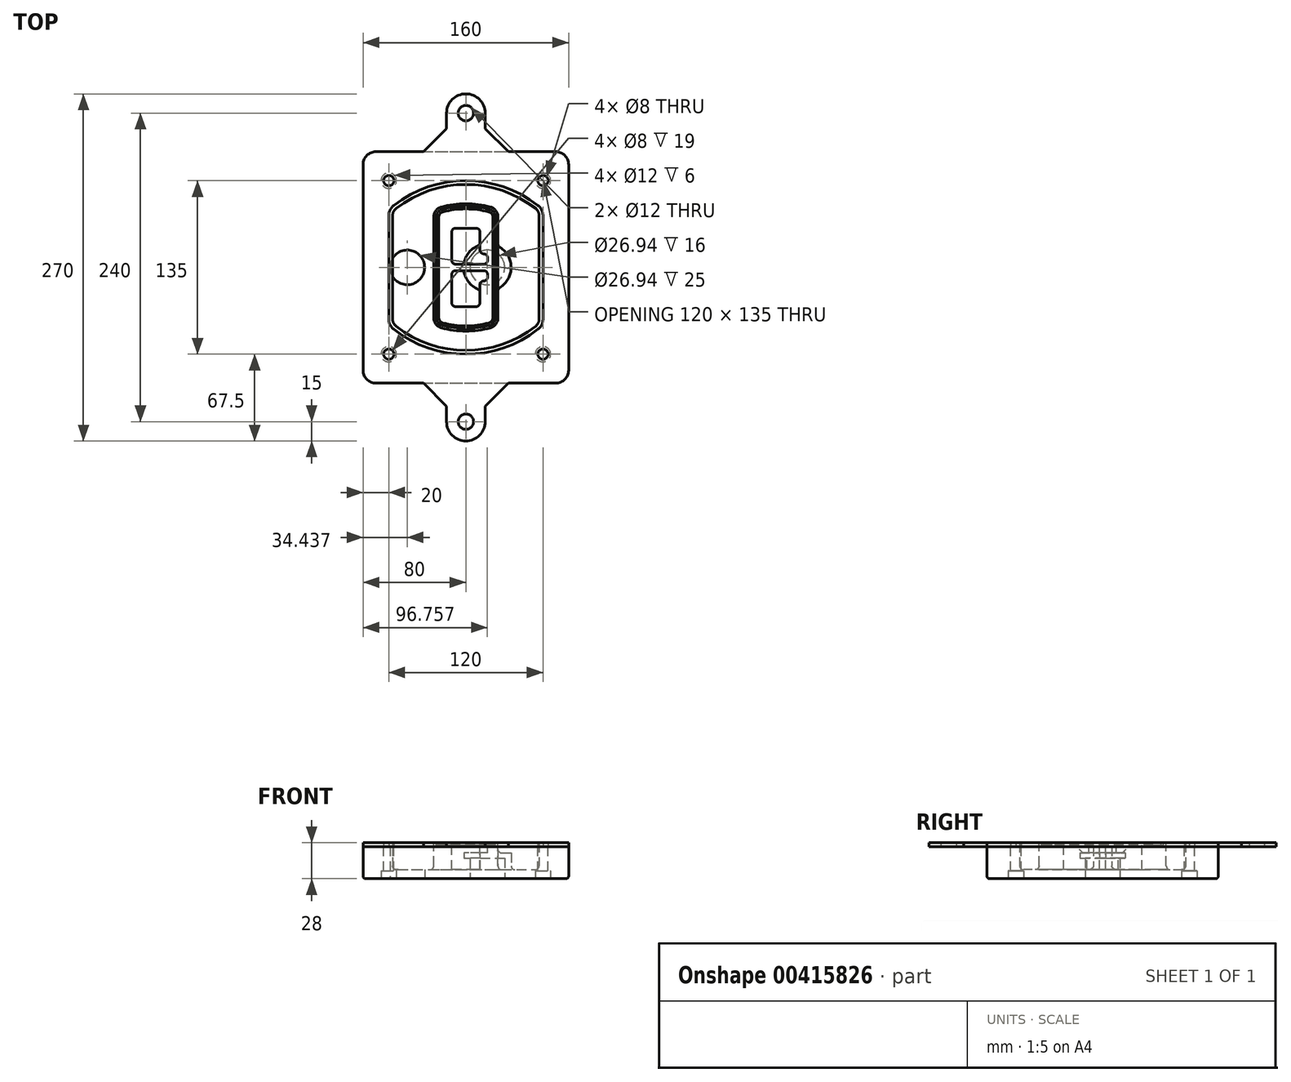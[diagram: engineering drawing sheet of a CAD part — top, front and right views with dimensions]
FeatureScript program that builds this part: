
annotation { "Feature Type Name" : "Feature", "Feature Type Description" : "" }
export const myFeature = defineFeature(function(context is Context, id is Id, definition is map)
    precondition{}
    {
        {
            var Q0;
            Q0=qCreatedBy(makeId("Top.planeOp"),FACE);
            var sketch = newSketch(context, id + "F0", { "sketchPlane" : qUnion([Q0])});
            skPoint(sketch, "E0.rect.middle", {"position": v(0, 0) * mm});
            skLineSegment(sketch, "E1.bottom", {"start": v(-70, -90) * mm, "end": v(70, -90) * mm});
            skLineSegment(sketch, "E1.top", {"start": v(-70, 90) * mm, "end": v(70, 90) * mm});
            skLineSegment(sketch, "E1.left", {"start": v(-80, -80) * mm, "end": v(-80, 80) * mm});
            skLineSegment(sketch, "E1.right", {"start": v(80, -80) * mm, "end": v(80, 80) * mm});
            skLineSegment(sketch, "E2", {"start": v(-80, 90) * mm, "end": v(80, -90) * mm, "construction": true});
            skLineSegment(sketch, "E3", {"start": v(80, 90) * mm, "end": v(-80, -90) * mm, "construction": true});
            skCircle(sketch, "E4", {"center": v(-60, 67.5) * mm, "radius": 4 * mm});
            skCircle(sketch, "E5", {"center": v(60, 67.5) * mm, "radius": 4 * mm});
            skCircle(sketch, "E6", {"center": v(60, -67.5) * mm, "radius": 4 * mm});
            skCircle(sketch, "E7", {"center": v(-60, -67.5) * mm, "radius": 4 * mm});
            skLineSegment(sketch, "E8", {"start": v(-60, 67.5) * mm, "end": v(60, 67.5) * mm, "construction": true});
            skLineSegment(sketch, "E9", {"start": v(60, 67.5) * mm, "end": v(60, -67.5) * mm, "construction": true});
            skLineSegment(sketch, "E10", {"start": v(60, -67.5) * mm, "end": v(-60, -67.5) * mm, "construction": true});
            skLineSegment(sketch, "E11", {"start": v(-60, -67.5) * mm, "end": v(-60, 67.5) * mm, "construction": true});
            skLineSegment(sketch, "E12", {"start": v(-60, 40.3) * mm, "end": v(-60, -40.3) * mm});
            skLineSegment(sketch, "E13", {"start": v(60, 40.3) * mm, "end": v(60, -40.3) * mm});
            skArc(sketch, "E14", {"start": v(56.15, 48.18) * mm, "mid": v(0, 67.5) * mm, "end": v(-56.15, 48.18) * mm});
            skArc(sketch, "E15", {"start": v(-56.15, -48.18) * mm, "mid": v(0, -67.5) * mm, "end": v(56.15, -48.18) * mm});
            skLineSegment(sketch, "E16", {"start": v(-60, 0) * mm, "end": v(60, 0) * mm, "construction": true});
            skPoint(sketch, "E17.visualSharp", {"position": v(-60, -45) * mm});
            skArc(sketch, "E17.filletArc", {"start": v(-60, -40.3) * mm, "mid": v(-58.99, -44.68) * mm, "end": v(-56.15, -48.18) * mm});
            skPoint(sketch, "E18.visualSharp", {"position": v(-60, 45) * mm});
            skArc(sketch, "E18.filletArc", {"start": v(-56.15, 48.18) * mm, "mid": v(-58.99, 44.68) * mm, "end": v(-60, 40.3) * mm});
            skPoint(sketch, "E19.visualSharp", {"position": v(60, 45) * mm});
            skArc(sketch, "E19.filletArc", {"start": v(60, 40.3) * mm, "mid": v(58.99, 44.68) * mm, "end": v(56.15, 48.18) * mm});
            skPoint(sketch, "E20.visualSharp", {"position": v(60, -45) * mm});
            skArc(sketch, "E20.filletArc", {"start": v(56.15, -48.18) * mm, "mid": v(58.99, -44.68) * mm, "end": v(60, -40.3) * mm});
            skPoint(sketch, "E21.visualSharp", {"position": v(-80, 90) * mm});
            skArc(sketch, "E21.filletArc", {"start": v(-70, 90) * mm, "mid": v(-77.07, 87.07) * mm, "end": v(-80, 80) * mm});
            skPoint(sketch, "E22.visualSharp", {"position": v(80, 90) * mm});
            skArc(sketch, "E22.filletArc", {"start": v(80, 80) * mm, "mid": v(77.07, 87.07) * mm, "end": v(70, 90) * mm});
            skPoint(sketch, "E23.visualSharp", {"position": v(80, -90) * mm});
            skArc(sketch, "E23.filletArc", {"start": v(70, -90) * mm, "mid": v(77.07, -87.07) * mm, "end": v(80, -80) * mm});
            skPoint(sketch, "E24.visualSharp", {"position": v(-80, -90) * mm});
            skArc(sketch, "E24.filletArc", {"start": v(-80, -80) * mm, "mid": v(-77.07, -87.07) * mm, "end": v(-70, -90) * mm});
            skArc(sketch, "E25.0", {"start": v(57, 40.3) * mm, "mid": v(56.3, 43.36) * mm, "end": v(54.3, 45.81) * mm});
            skLineSegment(sketch, "E25.1", {"start": v(57, 40.3) * mm, "end": v(57, -40.3) * mm});
            skArc(sketch, "E25.2", {"start": v(54.3, -45.81) * mm, "mid": v(56.3, -43.36) * mm, "end": v(57, -40.3) * mm});
            skArc(sketch, "E25.3", {"start": v(-54.3, -45.81) * mm, "mid": v(0, -64.5) * mm, "end": v(54.3, -45.81) * mm});
            skArc(sketch, "E25.4", {"start": v(-57, -40.3) * mm, "mid": v(-56.3, -43.36) * mm, "end": v(-54.3, -45.81) * mm});
            skArc(sketch, "E25.5", {"start": v(54.3, 45.81) * mm, "mid": v(0, 64.5) * mm, "end": v(-54.3, 45.81) * mm});
            skLineSegment(sketch, "E25.6", {"start": v(-57, 40.3) * mm, "end": v(-57, -40.3) * mm});
            skArc(sketch, "E25.7", {"start": v(-54.3, 45.81) * mm, "mid": v(-56.3, 43.36) * mm, "end": v(-57, 40.3) * mm});
            skArc(sketch, "E26.0", {"start": v(-58.62, 51.33) * mm, "mid": v(-62.58, 46.43) * mm, "end": v(-64, 40.3) * mm});
            skArc(sketch, "E26.1", {"start": v(58.62, 51.33) * mm, "mid": v(0, 71.5) * mm, "end": v(-58.62, 51.33) * mm});
            skArc(sketch, "E26.2", {"start": v(64, 40.3) * mm, "mid": v(62.58, 46.43) * mm, "end": v(58.62, 51.33) * mm});
            skLineSegment(sketch, "E26.3", {"start": v(64, 40.3) * mm, "end": v(64, -40.3) * mm});
            skArc(sketch, "E26.4", {"start": v(58.62, -51.33) * mm, "mid": v(62.58, -46.43) * mm, "end": v(64, -40.3) * mm});
            skLineSegment(sketch, "E26.5", {"start": v(-64, 40.3) * mm, "end": v(-64, -40.3) * mm});
            skArc(sketch, "E26.6", {"start": v(-58.62, -51.33) * mm, "mid": v(0, -71.5) * mm, "end": v(58.62, -51.33) * mm});
            skArc(sketch, "E26.7", {"start": v(-64, -40.3) * mm, "mid": v(-62.58, -46.43) * mm, "end": v(-58.62, -51.33) * mm});
            skSolve(sketch);
        }
        {
            var Q0;
            Q0=makeQuery(id+"F0.imprint","IMPRINT",FACE,{"disambiguationData":[TD([[makeQuery(id+"F0.imprint","IMPRINT",EDGE,{"derivedFrom":sQuery(id+"F0.wireOp",EDGE,"E1.bottom")}),1.0]])]});
            var Q1;
            Q1=makeQuery(id+"F0.imprint","IMPRINT",FACE,{"disambiguationData":[TD([[makeQuery(id+"F0.imprint","IMPRINT",EDGE,{"derivedFrom":sQuery(id+"F0.wireOp",EDGE,"E12")}),1.0]])]});
            var Q2;
            Q2=makeQuery(id+"F0.imprint","IMPRINT",FACE,{"disambiguationData":[TD([[makeQuery(id+"F0.imprint","IMPRINT",EDGE,{"derivedFrom":sQuery(id+"F0.wireOp",EDGE,"E25.0")}),1.0]])]});
            var Q3;
            Q3=makeQuery(id+"F0.imprint","IMPRINT",FACE,{"disambiguationData":[TD([[makeQuery(id+"F0.imprint","IMPRINT",EDGE,{"derivedFrom":sQuery(id+"F0.wireOp",EDGE,"E12")}),-1.0]])]});
            extrude(context, id + "F1", {"entities" : qUnion([Q0, Q1, Q2, Q3]), "oppositeDirection" : true, "depth" : 25 * mm});
        }
        {
            var Q0;
            Q0=makeQuery(id+"F0.imprint","IMPRINT",FACE,{"disambiguationData":[TD([[makeQuery(id+"F0.imprint","IMPRINT",EDGE,{"derivedFrom":sQuery(id+"F0.wireOp",EDGE,"E12")}),1.0]])]});
            extrude(context, id + "F2", {"entities" : qUnion([Q0]), "operationType" : NewBodyOperationType.ADD, "depth" : 3 * mm});
        }
        {
            var Q0;
            Q0=makeQuery(id+"F0.imprint","IMPRINT",FACE,{"disambiguationData":[TD([[makeQuery(id+"F0.imprint","IMPRINT",EDGE,{"derivedFrom":sQuery(id+"F0.wireOp",EDGE,"E25.0")}),1.0]])]});
            extrude(context, id + "F3", {"entities" : qUnion([Q0]), "operationType" : NewBodyOperationType.REMOVE, "oppositeDirection" : true, "depth" : 18 * mm});
        }
        {
            var Q0;
            Q0=makeQuery(id+"F2.opExtrude","CAP_FACE",FACE,{"disambiguationData":[OSD([sQuery(id+"F0.wireOp",EDGE,"E12"),sQuery(id+"F0.wireOp",EDGE,"E13"),sQuery(id+"F0.wireOp",EDGE,"E14"),sQuery(id+"F0.wireOp",EDGE,"E15"),sQuery(id+"F0.wireOp",EDGE,"E17.filletArc"),sQuery(id+"F0.wireOp",EDGE,"E18.filletArc"),sQuery(id+"F0.wireOp",EDGE,"E19.filletArc"),sQuery(id+"F0.wireOp",EDGE,"E20.filletArc"),sQuery(id+"F0.wireOp",EDGE,"E25.0"),sQuery(id+"F0.wireOp",EDGE,"E25.1"),sQuery(id+"F0.wireOp",EDGE,"E25.2"),sQuery(id+"F0.wireOp",EDGE,"E25.3"),sQuery(id+"F0.wireOp",EDGE,"E25.4"),sQuery(id+"F0.wireOp",EDGE,"E25.5"),sQuery(id+"F0.wireOp",EDGE,"E25.6"),sQuery(id+"F0.wireOp",EDGE,"E25.7")])],"isStart":false});
            var sketch = newSketch(context, id + "F4", { "sketchPlane" : qUnion([Q0])});
            skArc(sketch, "E27.0", {"start": v(-19.08, -46.97) * mm, "mid": v(0, -49.5) * mm, "end": v(19.08, -46.97) * mm});
            skArc(sketch, "E28.0", {"start": v(19.08, 46.97) * mm, "mid": v(0, 49.5) * mm, "end": v(-19.08, 46.97) * mm});
            skLineSegment(sketch, "E29", {"start": v(-25, 39.25) * mm, "end": v(-25, -39.25) * mm});
            skLineSegment(sketch, "E30", {"start": v(25, 39.25) * mm, "end": v(25, -39.25) * mm});
            skLineSegment(sketch, "E31", {"start": v(-25, 45.1) * mm, "end": v(25, 45.1) * mm, "construction": true});
            skLineSegment(sketch, "E32", {"start": v(-25, -45.1) * mm, "end": v(25, -45.1) * mm, "construction": true});
            skPoint(sketch, "E33.visualSharp", {"position": v(-25, 45.1) * mm});
            skArc(sketch, "E33.filletArc", {"start": v(-19.08, 46.97) * mm, "mid": v(-23.35, 44.11) * mm, "end": v(-25, 39.25) * mm});
            skPoint(sketch, "E34.visualSharp", {"position": v(25, 45.1) * mm});
            skArc(sketch, "E34.filletArc", {"start": v(25, 39.25) * mm, "mid": v(23.35, 44.11) * mm, "end": v(19.08, 46.97) * mm});
            skPoint(sketch, "E35.visualSharp", {"position": v(25, -45.1) * mm});
            skArc(sketch, "E35.filletArc", {"start": v(19.08, -46.97) * mm, "mid": v(23.35, -44.11) * mm, "end": v(25, -39.25) * mm});
            skPoint(sketch, "E36.visualSharp", {"position": v(-25, -45.1) * mm});
            skArc(sketch, "E36.filletArc", {"start": v(-25, -39.25) * mm, "mid": v(-23.35, -44.11) * mm, "end": v(-19.08, -46.97) * mm});
            skArc(sketch, "E37.0", {"start": v(54.3, 45.81) * mm, "mid": v(0, 64.5) * mm, "end": v(-54.3, 45.81) * mm});
            skArc(sketch, "E37.1", {"start": v(-54.3, 45.81) * mm, "mid": v(-56.3, 43.36) * mm, "end": v(-57, 40.3) * mm});
            skLineSegment(sketch, "E37.2", {"start": v(-57, 40.3) * mm, "end": v(-57, -40.3) * mm});
            skArc(sketch, "E37.3", {"start": v(-57, -40.3) * mm, "mid": v(-56.3, -43.36) * mm, "end": v(-54.3, -45.81) * mm});
            skArc(sketch, "E37.4", {"start": v(-54.3, -45.81) * mm, "mid": v(0, -64.5) * mm, "end": v(54.3, -45.81) * mm});
            skArc(sketch, "E37.5", {"start": v(54.3, -45.81) * mm, "mid": v(56.3, -43.36) * mm, "end": v(57, -40.3) * mm});
            skLineSegment(sketch, "E37.6", {"start": v(57, 40.3) * mm, "end": v(57, -40.3) * mm});
            skArc(sketch, "E37.7", {"start": v(57, 40.3) * mm, "mid": v(56.3, 43.36) * mm, "end": v(54.3, 45.81) * mm});
            skLineSegment(sketch, "E38.0", {"start": v(23, 39.25) * mm, "end": v(23, -39.25) * mm});
            skArc(sketch, "E38.1", {"start": v(18.56, -45.04) * mm, "mid": v(21.76, -42.9) * mm, "end": v(23, -39.25) * mm});
            skArc(sketch, "E38.2", {"start": v(-18.56, -45.04) * mm, "mid": v(0, -47.5) * mm, "end": v(18.56, -45.04) * mm});
            skArc(sketch, "E38.3", {"start": v(-23, -39.25) * mm, "mid": v(-21.76, -42.9) * mm, "end": v(-18.56, -45.04) * mm});
            skLineSegment(sketch, "E38.4", {"start": v(-23, 39.25) * mm, "end": v(-23, -39.25) * mm});
            skArc(sketch, "E38.5", {"start": v(23, 39.25) * mm, "mid": v(21.76, 42.9) * mm, "end": v(18.56, 45.04) * mm});
            skArc(sketch, "E38.6", {"start": v(-18.56, 45.04) * mm, "mid": v(-21.76, 42.9) * mm, "end": v(-23, 39.25) * mm});
            skArc(sketch, "E38.7", {"start": v(18.56, 45.04) * mm, "mid": v(0, 47.5) * mm, "end": v(-18.56, 45.04) * mm});
            skArc(sketch, "E39.0", {"start": v(21, 39.25) * mm, "mid": v(20.18, 41.68) * mm, "end": v(18.04, 43.1) * mm});
            skLineSegment(sketch, "E39.1", {"start": v(21, 39.25) * mm, "end": v(21, -39.25) * mm});
            skArc(sketch, "E39.2", {"start": v(18.04, -43.1) * mm, "mid": v(20.18, -41.68) * mm, "end": v(21, -39.25) * mm});
            skArc(sketch, "E39.3", {"start": v(-18.04, -43.1) * mm, "mid": v(0, -45.5) * mm, "end": v(18.04, -43.1) * mm});
            skArc(sketch, "E39.4", {"start": v(-21, -39.25) * mm, "mid": v(-20.18, -41.68) * mm, "end": v(-18.04, -43.1) * mm});
            skArc(sketch, "E39.5", {"start": v(18.04, 43.1) * mm, "mid": v(0, 45.5) * mm, "end": v(-18.04, 43.1) * mm});
            skLineSegment(sketch, "E39.6", {"start": v(-21, 39.25) * mm, "end": v(-21, -39.25) * mm});
            skArc(sketch, "E39.7", {"start": v(-18.04, 43.1) * mm, "mid": v(-20.18, 41.68) * mm, "end": v(-21, 39.25) * mm});
            skLineSegment(sketch, "E40", {"start": v(-25, 0) * mm, "end": v(25, 0) * mm, "construction": true});
            skLineSegment(sketch, "E41", {"start": v(-11, 5.5) * mm, "end": v(-11, 27.5) * mm});
            skLineSegment(sketch, "E42", {"start": v(-8, 30.5) * mm, "end": v(8, 30.5) * mm});
            skLineSegment(sketch, "E43", {"start": v(11, 27.5) * mm, "end": v(11, 13.5) * mm});
            skLineSegment(sketch, "E44", {"start": v(14, 10.5) * mm, "end": v(14, 10.5) * mm});
            skLineSegment(sketch, "E45", {"start": v(17, 7.5) * mm, "end": v(17, 5.5) * mm});
            skLineSegment(sketch, "E46", {"start": v(14, 2.5) * mm, "end": v(-8, 2.5) * mm});
            skPoint(sketch, "E47.visualSharp", {"position": v(-11, 30.5) * mm});
            skArc(sketch, "E47.filletArc", {"start": v(-8, 30.5) * mm, "mid": v(-10.12, 29.62) * mm, "end": v(-11, 27.5) * mm});
            skPoint(sketch, "E48.visualSharp", {"position": v(11, 30.5) * mm});
            skArc(sketch, "E48.filletArc", {"start": v(11, 27.5) * mm, "mid": v(10.12, 29.62) * mm, "end": v(8, 30.5) * mm});
            skPoint(sketch, "E49.visualSharp", {"position": v(11, 10.5) * mm});
            skArc(sketch, "E49.filletArc", {"start": v(11, 13.5) * mm, "mid": v(11.88, 11.38) * mm, "end": v(14, 10.5) * mm});
            skPoint(sketch, "E50.visualSharp", {"position": v(17, 10.5) * mm});
            skArc(sketch, "E50.filletArc", {"start": v(17, 7.5) * mm, "mid": v(16.12, 9.62) * mm, "end": v(14, 10.5) * mm});
            skPoint(sketch, "E51.visualSharp", {"position": v(17, 2.5) * mm});
            skArc(sketch, "E51.filletArc", {"start": v(14, 2.5) * mm, "mid": v(16.12, 3.38) * mm, "end": v(17, 5.5) * mm});
            skPoint(sketch, "E52.visualSharp", {"position": v(-11, 2.5) * mm});
            skArc(sketch, "E52.filletArc", {"start": v(-11, 5.5) * mm, "mid": v(-10.12, 3.38) * mm, "end": v(-8, 2.5) * mm});
            skLineSegment(sketch, "E53.0.MirrorCS", {"start": v(14, -2.5) * mm, "end": v(-8, -2.5) * mm});
            skArc(sketch, "E54.0.MirrorCS", {"start": v(-11, -5.5) * mm, "mid": v(-10.12, -3.38) * mm, "end": v(-8, -2.5) * mm});
            skLineSegment(sketch, "E55.0.MirrorCS", {"start": v(-11, -5.5) * mm, "end": v(-11, -27.5) * mm});
            skArc(sketch, "E56.0.MirrorCS", {"start": v(-8, -30.5) * mm, "mid": v(-10.12, -29.62) * mm, "end": v(-11, -27.5) * mm});
            skLineSegment(sketch, "E57.0.MirrorCS", {"start": v(-8, -30.5) * mm, "end": v(8, -30.5) * mm});
            skArc(sketch, "E58.0.MirrorCS", {"start": v(11, -27.5) * mm, "mid": v(10.12, -29.62) * mm, "end": v(8, -30.5) * mm});
            skLineSegment(sketch, "E59.0.MirrorCS", {"start": v(11, -27.5) * mm, "end": v(11, -13.5) * mm});
            skArc(sketch, "E60.0.MirrorCS", {"start": v(11, -13.5) * mm, "mid": v(11.88, -11.38) * mm, "end": v(14, -10.5) * mm});
            skArc(sketch, "E61.0.MirrorCS", {"start": v(17, -7.5) * mm, "mid": v(16.12, -9.62) * mm, "end": v(14, -10.5) * mm});
            skLineSegment(sketch, "E62.0.MirrorCS", {"start": v(17, -7.5) * mm, "end": v(17, -5.5) * mm});
            skArc(sketch, "E63.0.MirrorCS", {"start": v(14, -2.5) * mm, "mid": v(16.12, -3.38) * mm, "end": v(17, -5.5) * mm});
            skSolve(sketch);
        }
        {
            var Q0;
            Q0=makeQuery(id+"F4.imprint","IMPRINT",FACE,{"disambiguationData":[TD([[makeQuery(id+"F4.imprint","IMPRINT",EDGE,{"derivedFrom":sQuery(id+"F4.wireOp",EDGE,"E27.0")}),1.0]])]});
            var Q1;
            Q1=makeQuery(id+"F4.imprint","IMPRINT",FACE,{"disambiguationData":[TD([[makeQuery(id+"F4.imprint","IMPRINT",EDGE,{"derivedFrom":sQuery(id+"F4.wireOp",EDGE,"E38.0")}),-1.0]])]});
            var Q2;
            Q2=makeQuery(id+"F4.imprint","IMPRINT",FACE,{"disambiguationData":[TD([[makeQuery(id+"F4.imprint","IMPRINT",EDGE,{"derivedFrom":sQuery(id+"F4.wireOp",EDGE,"E39.0")}),1.0]])]});
            extrude(context, id + "F5", {"entities" : qUnion([Q0, Q1, Q2]), "operationType" : NewBodyOperationType.ADD, "endBound" : BoundingType.UP_TO_NEXT, "oppositeDirection" : true, "depth" : 25 * mm});
        }
        {
            var Q0;
            Q0=makeQuery(id+"F4.imprint","IMPRINT",FACE,{"disambiguationData":[TD([[makeQuery(id+"F4.imprint","IMPRINT",EDGE,{"derivedFrom":sQuery(id+"F4.wireOp",EDGE,"E38.0")}),-1.0]])]});
            extrude(context, id + "F6", {"entities" : qUnion([Q0]), "operationType" : NewBodyOperationType.REMOVE, "oppositeDirection" : true, "depth" : 2 * mm});
        }
        {
            var Q0;
            Q0=makeQuery(id+"F1.opExtrude","CAP_FACE",FACE,{"disambiguationData":[OSD([sQuery(id+"F0.wireOp",EDGE,"E1.bottom"),sQuery(id+"F0.wireOp",EDGE,"E1.top"),sQuery(id+"F0.wireOp",EDGE,"E1.left"),sQuery(id+"F0.wireOp",EDGE,"E1.right"),sQuery(id+"F0.wireOp",EDGE,"E4"),sQuery(id+"F0.wireOp",EDGE,"E5"),sQuery(id+"F0.wireOp",EDGE,"E6"),sQuery(id+"F0.wireOp",EDGE,"E7"),sQuery(id+"F0.wireOp",EDGE,"E21.filletArc"),sQuery(id+"F0.wireOp",EDGE,"E22.filletArc"),sQuery(id+"F0.wireOp",EDGE,"E23.filletArc"),sQuery(id+"F0.wireOp",EDGE,"E24.filletArc")])],"isStart":false});
            var sketch = newSketch(context, id + "F7", { "sketchPlane" : qUnion([Q0])});
            skCircle(sketch, "E64", {"center": v(16.76, 0) * mm, "radius": 13.47 * mm});
            skCircle(sketch, "E65", {"center": v(-45.56, 0) * mm, "radius": 13.47 * mm});
            skLineSegment(sketch, "E66", {"start": v(80, 0) * mm, "end": v(-80, 0) * mm});
            skCircle(sketch, "E67", {"center": v(16.76, 0) * mm, "radius": 18.47 * mm});
            skCircle(sketch, "E68", {"center": v(60, -67.5) * mm, "radius": 6 * mm});
            skCircle(sketch, "E69", {"center": v(-60, -67.5) * mm, "radius": 6 * mm});
            skCircle(sketch, "E70", {"center": v(-60, 67.5) * mm, "radius": 6 * mm});
            skCircle(sketch, "E71", {"center": v(60, 67.5) * mm, "radius": 6 * mm});
            skSolve(sketch);
        }
        {
            var Q0;
            {var subQ1=sQuery(id+"F7.wireOp",EDGE,"E66");var subQ4=sQuery(id+"F7.wireOp",EDGE,"E64");var subQ6=makeQuery(id+"F7.imprint","INTERSECT",VERTEX,{"disambiguationData":[OD(0.0)],"derivedFrom":[subQ4,subQ1]});Q0=makeQuery(id+"F7.imprint","IMPRINT",FACE,{"disambiguationData":[TD([[makeQuery(id+"F7.imprint","IMPRINT",EDGE,{"disambiguationData":[TD([[subQ6,-1.0]])],"derivedFrom":subQ4}),-1.0]])]});}
            var Q1;
            {var subQ0=sQuery(id+"F7.wireOp",EDGE,"E66");var subQ1=sQuery(id+"F7.wireOp",EDGE,"E64");var subQ3=makeQuery(id+"F7.imprint","INTERSECT",VERTEX,{"disambiguationData":[OD(0.0)],"derivedFrom":[subQ1,subQ0]});Q1=makeQuery(id+"F7.imprint","IMPRINT",FACE,{"disambiguationData":[TD([[makeQuery(id+"F7.imprint","IMPRINT",EDGE,{"disambiguationData":[TD([[subQ3,-1.0]])],"derivedFrom":subQ1}),1.0]])]});}
            var Q2;
            {var subQ0=sQuery(id+"F7.wireOp",EDGE,"E66");var subQ1=sQuery(id+"F7.wireOp",EDGE,"E64");var subQ3=makeQuery(id+"F7.imprint","INTERSECT",VERTEX,{"disambiguationData":[OD(0.0)],"derivedFrom":[subQ1,subQ0]});Q2=makeQuery(id+"F7.imprint","IMPRINT",FACE,{"disambiguationData":[TD([[makeQuery(id+"F7.imprint","IMPRINT",EDGE,{"disambiguationData":[TD([[subQ3,1.0]])],"derivedFrom":subQ1}),1.0]])]});}
            var Q3;
            {var subQ1=sQuery(id+"F7.wireOp",EDGE,"E66");var subQ4=sQuery(id+"F7.wireOp",EDGE,"E64");var subQ6=makeQuery(id+"F7.imprint","INTERSECT",VERTEX,{"disambiguationData":[OD(0.0)],"derivedFrom":[subQ4,subQ1]});Q3=makeQuery(id+"F7.imprint","IMPRINT",FACE,{"disambiguationData":[TD([[makeQuery(id+"F7.imprint","IMPRINT",EDGE,{"disambiguationData":[TD([[subQ6,1.0]])],"derivedFrom":subQ4}),-1.0]])]});}
            extrude(context, id + "F8", {"entities" : qUnion([Q0, Q1, Q2, Q3]), "operationType" : NewBodyOperationType.ADD, "oppositeDirection" : true, "depth" : 20 * mm});
        }
        {
            var Q0;
            {var subQ0=sQuery(id+"F7.wireOp",EDGE,"E66");var subQ1=sQuery(id+"F7.wireOp",EDGE,"E64");var subQ3=makeQuery(id+"F7.imprint","INTERSECT",VERTEX,{"disambiguationData":[OD(0.0)],"derivedFrom":[subQ1,subQ0]});Q0=makeQuery(id+"F7.imprint","IMPRINT",FACE,{"disambiguationData":[TD([[makeQuery(id+"F7.imprint","IMPRINT",EDGE,{"disambiguationData":[TD([[subQ3,-1.0]])],"derivedFrom":subQ1}),1.0]])]});}
            var Q1;
            {var subQ0=sQuery(id+"F7.wireOp",EDGE,"E66");var subQ1=sQuery(id+"F7.wireOp",EDGE,"E64");var subQ3=makeQuery(id+"F7.imprint","INTERSECT",VERTEX,{"disambiguationData":[OD(0.0)],"derivedFrom":[subQ1,subQ0]});Q1=makeQuery(id+"F7.imprint","IMPRINT",FACE,{"disambiguationData":[TD([[makeQuery(id+"F7.imprint","IMPRINT",EDGE,{"disambiguationData":[TD([[subQ3,1.0]])],"derivedFrom":subQ1}),1.0]])]});}
            extrude(context, id + "F9", {"entities" : qUnion([Q0, Q1]), "operationType" : NewBodyOperationType.REMOVE, "oppositeDirection" : true, "depth" : 16 * mm});
        }
        {
            var Q0;
            {var subQ0=sQuery(id+"F7.wireOp",EDGE,"E66");var subQ1=sQuery(id+"F7.wireOp",EDGE,"E65");var subQ3=makeQuery(id+"F7.imprint","INTERSECT",VERTEX,{"disambiguationData":[OD(0.0)],"derivedFrom":[subQ1,subQ0]});Q0=makeQuery(id+"F7.imprint","IMPRINT",FACE,{"disambiguationData":[TD([[makeQuery(id+"F7.imprint","IMPRINT",EDGE,{"disambiguationData":[TD([[subQ3,-1.0]])],"derivedFrom":subQ1}),1.0]])]});}
            var Q1;
            {var subQ0=sQuery(id+"F7.wireOp",EDGE,"E66");var subQ1=sQuery(id+"F7.wireOp",EDGE,"E65");var subQ3=makeQuery(id+"F7.imprint","INTERSECT",VERTEX,{"disambiguationData":[OD(0.0)],"derivedFrom":[subQ1,subQ0]});Q1=makeQuery(id+"F7.imprint","IMPRINT",FACE,{"disambiguationData":[TD([[makeQuery(id+"F7.imprint","IMPRINT",EDGE,{"disambiguationData":[TD([[subQ3,1.0]])],"derivedFrom":subQ1}),1.0]])]});}
            extrude(context, id + "F10", {"entities" : qUnion([Q0, Q1]), "operationType" : NewBodyOperationType.REMOVE, "oppositeDirection" : true, "depth" : 25 * mm});
        }
        {
            var Q0;
            Q0=makeQuery(id+"F7.imprint","IMPRINT",FACE,{"disambiguationData":[TD([[makeQuery(id+"F7.imprint","IMPRINT",EDGE,{"derivedFrom":sQuery(id+"F7.wireOp",EDGE,"E68")}),1.0]])]});
            var Q1;
            Q1=makeQuery(id+"F7.imprint","IMPRINT",FACE,{"disambiguationData":[TD([[makeQuery(id+"F7.imprint","IMPRINT",EDGE,{"derivedFrom":makeQuery(id+"F1.opExtrude","CAP_EDGE",EDGE,{"disambiguationData":[OSD([sQuery(id+"F0.wireOp",EDGE,"E5")])],"isStart":false})}),-1.0]])]});
            var Q2;
            Q2=makeQuery(id+"F7.imprint","IMPRINT",FACE,{"disambiguationData":[TD([[makeQuery(id+"F7.imprint","IMPRINT",EDGE,{"derivedFrom":sQuery(id+"F7.wireOp",EDGE,"E69")}),1.0]])]});
            var Q3;
            Q3=makeQuery(id+"F7.imprint","IMPRINT",FACE,{"disambiguationData":[TD([[makeQuery(id+"F7.imprint","IMPRINT",EDGE,{"derivedFrom":makeQuery(id+"F1.opExtrude","CAP_EDGE",EDGE,{"disambiguationData":[OSD([sQuery(id+"F0.wireOp",EDGE,"E4")])],"isStart":false})}),-1.0]])]});
            var Q4;
            Q4=makeQuery(id+"F7.imprint","IMPRINT",FACE,{"disambiguationData":[TD([[makeQuery(id+"F7.imprint","IMPRINT",EDGE,{"derivedFrom":sQuery(id+"F7.wireOp",EDGE,"E70")}),1.0]])]});
            var Q5;
            Q5=makeQuery(id+"F7.imprint","IMPRINT",FACE,{"disambiguationData":[TD([[makeQuery(id+"F7.imprint","IMPRINT",EDGE,{"derivedFrom":makeQuery(id+"F1.opExtrude","CAP_EDGE",EDGE,{"disambiguationData":[OSD([sQuery(id+"F0.wireOp",EDGE,"E7")])],"isStart":false})}),-1.0]])]});
            var Q6;
            Q6=makeQuery(id+"F7.imprint","IMPRINT",FACE,{"disambiguationData":[TD([[makeQuery(id+"F7.imprint","IMPRINT",EDGE,{"derivedFrom":sQuery(id+"F7.wireOp",EDGE,"E71")}),1.0]])]});
            var Q7;
            Q7=makeQuery(id+"F7.imprint","IMPRINT",FACE,{"disambiguationData":[TD([[makeQuery(id+"F7.imprint","IMPRINT",EDGE,{"derivedFrom":makeQuery(id+"F1.opExtrude","CAP_EDGE",EDGE,{"disambiguationData":[OSD([sQuery(id+"F0.wireOp",EDGE,"E6")])],"isStart":false})}),-1.0]])]});
            extrude(context, id + "F11", {"entities" : qUnion([Q0, Q1, Q2, Q3, Q4, Q5, Q6, Q7]), "operationType" : NewBodyOperationType.REMOVE, "oppositeDirection" : true, "depth" : 6 * mm});
        }
        {
            var Q0;
            Q0=makeQuery(id+"F9.boolean.opBoolean","COPY",FACE,{"derivedFrom":makeQuery(id+"F9.opExtrude","CAP_FACE",FACE,{"disambiguationData":[OSD([sQuery(id+"F7.wireOp",EDGE,"E64")])],"isStart":false})});
            var sketch = newSketch(context, id + "F12", { "sketchPlane" : qUnion([Q0])});
            skArc(sketch, "E72.0", {"start": v(11, 17.55) * mm, "mid": v(2.57, 11.82) * mm, "end": v(-1.54, 2.5) * mm});
            skArc(sketch, "E72.1", {"start": v(-1.54, -2.5) * mm, "mid": v(2.57, -11.82) * mm, "end": v(11, -17.55) * mm});
            skLineSegment(sketch, "E73", {"start": v(-1.54, -2.5) * mm, "end": v(14, -2.5) * mm});
            skLineSegment(sketch, "E74.0", {"start": v(14, 2.5) * mm, "end": v(-1.54, 2.5) * mm});
            skArc(sketch, "E74.1", {"start": v(14, 2.5) * mm, "mid": v(16.12, 3.38) * mm, "end": v(17, 5.5) * mm});
            skLineSegment(sketch, "E74.2", {"start": v(17, 7.5) * mm, "end": v(17, 5.5) * mm});
            skArc(sketch, "E74.3", {"start": v(17, 7.5) * mm, "mid": v(16.12, 9.62) * mm, "end": v(14, 10.5) * mm});
            skArc(sketch, "E74.4", {"start": v(11, 13.5) * mm, "mid": v(11.88, 11.38) * mm, "end": v(14, 10.5) * mm});
            skLineSegment(sketch, "E74.5", {"start": v(11, 17.55) * mm, "end": v(11, 13.5) * mm});
            skLineSegment(sketch, "E74.7", {"start": v(14, -2.5) * mm, "end": v(-1.54, -2.5) * mm});
            skArc(sketch, "E74.8", {"start": v(14, -2.5) * mm, "mid": v(16.12, -3.38) * mm, "end": v(17, -5.5) * mm});
            skLineSegment(sketch, "E74.9", {"start": v(17, -7.5) * mm, "end": v(17, -5.5) * mm});
            skArc(sketch, "E74.10", {"start": v(17, -7.5) * mm, "mid": v(16.12, -9.62) * mm, "end": v(14, -10.5) * mm});
            skArc(sketch, "E74.11", {"start": v(11, -13.5) * mm, "mid": v(11.88, -11.38) * mm, "end": v(14, -10.5) * mm});
            skLineSegment(sketch, "E74.12", {"start": v(11, -17.55) * mm, "end": v(11, -13.5) * mm});
            skPoint(sketch, "E75.orphan", {"position": v(11, -27.5) * mm});
            skPoint(sketch, "E76.orphan", {"position": v(-8, -2.5) * mm});
            skPoint(sketch, "E77.orphan", {"position": v(-8, 2.5) * mm});
            skPoint(sketch, "E78.orphan", {"position": v(11, 27.5) * mm});
            skSolve(sketch);
        }
        {
            var Q0;
            {var subQ7=sQuery(id+"F12.wireOp",EDGE,"E72.0");var subQ14=sQuery(id+"F12.wireOp",EDGE,"E72.1");var subQ16=sQuery(id+"F12.wireOp",EDGE,"E74.1");var subQ18=sQuery(id+"F12.wireOp",EDGE,"E74.8");Q0=qUnion([makeQuery(id+"F12.imprint","IMPRINT",FACE,{"disambiguationData":[TD([[makeQuery(id+"F12.imprint","IMPRINT",EDGE,{"derivedFrom":subQ7}),1.0]])]}),makeQuery(id+"F12.imprint","IMPRINT",FACE,{"disambiguationData":[TD([[makeQuery(id+"F12.imprint","IMPRINT",EDGE,{"derivedFrom":subQ14}),1.0]])]}),makeQuery(id+"F12.imprint","IMPRINT",FACE,{"disambiguationData":[TD([[makeQuery(id+"F12.imprint","IMPRINT",EDGE,{"derivedFrom":subQ16}),1.0]])]}),makeQuery(id+"F12.imprint","IMPRINT",FACE,{"disambiguationData":[TD([[makeQuery(id+"F12.imprint","IMPRINT",EDGE,{"derivedFrom":subQ18}),-1.0]])]})]);}
            var Q1;
            Q1=makeQuery(id+"F5.boolean.opBoolean","SPLIT",FACE,{"disambiguationData":[TD([makeQuery(id+"F5.opExtrude","SWEPT_FACE",FACE,{"disambiguationData":[OSD([sQuery(id+"F4.wireOp",EDGE,"E41")])]})])],"derivedFrom":makeQuery(id+"F3.boolean.opBoolean","COPY",FACE,{"derivedFrom":makeQuery(id+"F3.opExtrude","CAP_FACE",FACE,{"disambiguationData":[OSD([sQuery(id+"F0.wireOp",EDGE,"E25.0"),sQuery(id+"F0.wireOp",EDGE,"E25.1"),sQuery(id+"F0.wireOp",EDGE,"E25.2"),sQuery(id+"F0.wireOp",EDGE,"E25.3"),sQuery(id+"F0.wireOp",EDGE,"E25.4"),sQuery(id+"F0.wireOp",EDGE,"E25.5"),sQuery(id+"F0.wireOp",EDGE,"E25.6"),sQuery(id+"F0.wireOp",EDGE,"E25.7")])],"isStart":false})})});
            extrude(context, id + "F13", {"entities" : qUnion([Q0]), "operationType" : NewBodyOperationType.REMOVE, "endBound" : BoundingType.UP_TO_SURFACE, "endBoundEntityFace" : qUnion([Q1]), "depth" : 25 * mm});
        }
        {
            var Q0;
            Q0=makeQuery(id+"F3.boolean.opBoolean","COPY",EDGE,{"derivedFrom":makeQuery(id+"F3.opExtrude","CAP_EDGE",EDGE,{"disambiguationData":[OSD([sQuery(id+"F0.wireOp",EDGE,"E25.6")])],"isStart":false})});
            var Q1;
            Q1=makeQuery(id+"F8.boolean.opBoolean","INTERSECT",EDGE,{"derivedFrom":[makeQuery(id+"F5.opExtrude","SWEPT_FACE",FACE,{"disambiguationData":[OSD([sQuery(id+"F4.wireOp",EDGE,"E30")])]}),makeQuery(id+"F8.opExtrude","CAP_FACE",FACE,{"disambiguationData":[OSD([sQuery(id+"F7.wireOp",EDGE,"E67")])],"isStart":false})]});
            var Q2;
            Q2=makeQuery(id+"F8.boolean.opBoolean","INTERSECT",EDGE,{"disambiguationData":[OD(1.0)],"derivedFrom":[makeQuery(id+"F5.opExtrude","SWEPT_FACE",FACE,{"disambiguationData":[OSD([sQuery(id+"F4.wireOp",EDGE,"E30")])]}),makeQuery(id+"F8.opExtrude","SWEPT_FACE",FACE,{"disambiguationData":[OSD([sQuery(id+"F7.wireOp",EDGE,"E67")])]})]});
            var Q3;
            {var subQ0=sQuery(id+"F4.wireOp",EDGE,"E30");Q3=makeQuery(id+"F8.boolean.opBoolean","SPLIT",EDGE,{"disambiguationData":[TD([makeQuery(id+"F5.opExtrude","SWEPT_FACE",FACE,{"disambiguationData":[OSD([sQuery(id+"F4.wireOp",EDGE,"E35.filletArc")])]})])],"derivedFrom":makeQuery(id+"F5.opExtrude","CAP_EDGE",EDGE,{"disambiguationData":[OSD([subQ0])],"isStart":false})});}
            var Q4;
            {var subQ0=sQuery(id+"F0.wireOp",EDGE,"E25.7");var subQ1=sQuery(id+"F0.wireOp",EDGE,"E25.1");var subQ2=sQuery(id+"F0.wireOp",EDGE,"E25.6");var subQ3=sQuery(id+"F0.wireOp",EDGE,"E25.5");var subQ4=sQuery(id+"F0.wireOp",EDGE,"E25.4");var subQ5=sQuery(id+"F0.wireOp",EDGE,"E25.0");var subQ6=sQuery(id+"F0.wireOp",EDGE,"E25.2");var subQ7=sQuery(id+"F0.wireOp",EDGE,"E25.3");Q4=makeQuery(id+"F8.boolean.opBoolean","INTERSECT",EDGE,{"derivedFrom":[makeQuery(id+"F5.boolean.opBoolean","SPLIT",FACE,{"disambiguationData":[TD([makeQuery(id+"F2.opExtrude","SWEPT_FACE",FACE,{"disambiguationData":[OSD([subQ5])]})])],"derivedFrom":makeQuery(id+"F3.boolean.opBoolean","COPY",FACE,{"derivedFrom":makeQuery(id+"F3.opExtrude","CAP_FACE",FACE,{"disambiguationData":[OSD([subQ5,subQ1,subQ6,subQ7,subQ4,subQ3,subQ2,subQ0])],"isStart":false})})}),makeQuery(id+"F8.opExtrude","SWEPT_FACE",FACE,{"disambiguationData":[OSD([sQuery(id+"F7.wireOp",EDGE,"E67")])]})]});}
            var Q5;
            Q5=makeQuery(id+"F8.boolean.opBoolean","INTERSECT",EDGE,{"disambiguationData":[OD(0.0)],"derivedFrom":[makeQuery(id+"F5.opExtrude","SWEPT_FACE",FACE,{"disambiguationData":[OSD([sQuery(id+"F4.wireOp",EDGE,"E30")])]}),makeQuery(id+"F8.opExtrude","SWEPT_FACE",FACE,{"disambiguationData":[OSD([sQuery(id+"F7.wireOp",EDGE,"E67")])]})]});
            fillet(context, id + "F14", {"entities" : qUnion([Q0, Q1, Q2, Q3, Q4, Q5]), "radius" : 3 * mm, "tangentPropagation" : true, "allowEdgeOverflow" : false});
        }
        {
            var Q0;
            Q0=makeQuery(id+"F1.opExtrude","CAP_EDGE",EDGE,{"disambiguationData":[OSD([sQuery(id+"F0.wireOp",EDGE,"E1.bottom")])],"isStart":false});
            fillet(context, id + "F15", {"entities" : qUnion([Q0]), "radius" : 2 * mm, "tangentPropagation" : true, "allowEdgeOverflow" : false});
        }
        {
            var Q0;
            {var subQ0=sQuery(id+"F0.wireOp",EDGE,"E21.filletArc");var subQ1=sQuery(id+"F0.wireOp",EDGE,"E7");var subQ2=sQuery(id+"F0.wireOp",EDGE,"E6");var subQ3=sQuery(id+"F0.wireOp",EDGE,"E5");var subQ4=sQuery(id+"F0.wireOp",EDGE,"E4");var subQ5=sQuery(id+"F0.wireOp",EDGE,"E22.filletArc");var subQ6=sQuery(id+"F0.wireOp",EDGE,"E1.bottom");var subQ7=sQuery(id+"F0.wireOp",EDGE,"E1.right");var subQ8=sQuery(id+"F0.wireOp",EDGE,"E1.top");var subQ9=sQuery(id+"F0.wireOp",EDGE,"E1.left");var subQ10=sQuery(id+"F0.wireOp",EDGE,"E23.filletArc");var subQ11=sQuery(id+"F0.wireOp",EDGE,"E24.filletArc");Q0=makeQuery(id+"F2.boolean.opBoolean","SPLIT",FACE,{"disambiguationData":[TD([makeQuery(id+"F1.opExtrude","SWEPT_FACE",FACE,{"disambiguationData":[OSD([subQ6])]})])],"derivedFrom":makeQuery(id+"F1.opExtrude","CAP_FACE",FACE,{"disambiguationData":[OSD([subQ6,subQ8,subQ9,subQ7,subQ4,subQ3,subQ2,subQ1,subQ0,subQ5,subQ10,subQ11])],"isStart":true})});}
            var sketch = newSketch(context, id + "F16", { "sketchPlane" : qUnion([Q0])});
            skLineSegment(sketch, "E79", {"start": v(0, 90) * mm, "end": v(0, 90) * mm});
            skLineSegment(sketch, "E80", {"start": v(0, 90) * mm, "end": v(0, 120) * mm, "construction": true});
            skCircle(sketch, "E81", {"center": v(0, 120) * mm, "radius": 6 * mm});
            skArc(sketch, "E82", {"start": v(15, 120) * mm, "mid": v(0, 135) * mm, "end": v(-15, 120) * mm});
            skLineSegment(sketch, "E83", {"start": v(-15, 120) * mm, "end": v(-15, 108) * mm});
            skLineSegment(sketch, "E84", {"start": v(-15, 108) * mm, "end": v(-33, 90) * mm});
            skLineSegment(sketch, "E85", {"start": v(15, 120) * mm, "end": v(15, 108) * mm});
            skLineSegment(sketch, "E86", {"start": v(15, 108) * mm, "end": v(33, 90) * mm});
            skLineSegment(sketch, "E87", {"start": v(-80, 0) * mm, "end": v(80, 0) * mm, "construction": true});
            skLineSegment(sketch, "E88.MirrorCS", {"start": v(15, -108) * mm, "end": v(33, -90) * mm});
            skLineSegment(sketch, "E89.MirrorCS", {"start": v(15, -120) * mm, "end": v(15, -108) * mm});
            skArc(sketch, "E90.MirrorCS", {"start": v(15, -120) * mm, "mid": v(0, -135) * mm, "end": v(-15, -120) * mm});
            skCircle(sketch, "E91.MirrorC", {"center": v(0, -120) * mm, "radius": 6 * mm});
            skLineSegment(sketch, "E92.MirrorCS", {"start": v(-15, -120) * mm, "end": v(-15, -108) * mm});
            skLineSegment(sketch, "E93.MirrorCS", {"start": v(-15, -108) * mm, "end": v(-33, -90) * mm});
            skLineSegment(sketch, "E94.MirrorCS", {"start": v(0, -90) * mm, "end": v(0, -120) * mm, "construction": true});
            skSolve(sketch);
        }
        {
            var Q0;
            Q0=makeQuery(id+"F16.imprint","IMPRINT",FACE,{"disambiguationData":[TD([[makeQuery(id+"F16.imprint","IMPRINT",EDGE,{"derivedFrom":makeQuery(id+"F1.opExtrude","CAP_EDGE",EDGE,{"disambiguationData":[OSD([sQuery(id+"F0.wireOp",EDGE,"E1.left")])],"isStart":true})}),-1.0]])]});
            var Q1;
            {var subQ0=sQuery(id+"F16.wireOp",EDGE,"E88.MirrorCS");Q1=makeQuery(id+"F16.imprint","IMPRINT",FACE,{"disambiguationData":[TD([[makeQuery(id+"F16.imprint","IMPRINT",EDGE,{"derivedFrom":subQ0}),1.0]])]});}
            var Q2;
            Q2=makeQuery(id+"F16.imprint","IMPRINT",FACE,{"disambiguationData":[TD([[makeQuery(id+"F16.imprint","IMPRINT",EDGE,{"derivedFrom":sQuery(id+"F16.wireOp",EDGE,"E81")}),-1.0]])]});
            var Q3;
            Q3=makeQuery(id+"F2.opExtrude","CAP_FACE",FACE,{"disambiguationData":[OSD([sQuery(id+"F0.wireOp",EDGE,"E12"),sQuery(id+"F0.wireOp",EDGE,"E13"),sQuery(id+"F0.wireOp",EDGE,"E14"),sQuery(id+"F0.wireOp",EDGE,"E15"),sQuery(id+"F0.wireOp",EDGE,"E17.filletArc"),sQuery(id+"F0.wireOp",EDGE,"E18.filletArc"),sQuery(id+"F0.wireOp",EDGE,"E19.filletArc"),sQuery(id+"F0.wireOp",EDGE,"E20.filletArc"),sQuery(id+"F0.wireOp",EDGE,"E25.0"),sQuery(id+"F0.wireOp",EDGE,"E25.1"),sQuery(id+"F0.wireOp",EDGE,"E25.2"),sQuery(id+"F0.wireOp",EDGE,"E25.3"),sQuery(id+"F0.wireOp",EDGE,"E25.4"),sQuery(id+"F0.wireOp",EDGE,"E25.5"),sQuery(id+"F0.wireOp",EDGE,"E25.6"),sQuery(id+"F0.wireOp",EDGE,"E25.7")])],"isStart":false});
            extrude(context, id + "F17", {"entities" : qUnion([Q0, Q1, Q2]), "endBound" : BoundingType.UP_TO_SURFACE, "endBoundEntityFace" : qUnion([Q3]), "depth" : 25 * mm});
        }
    });
